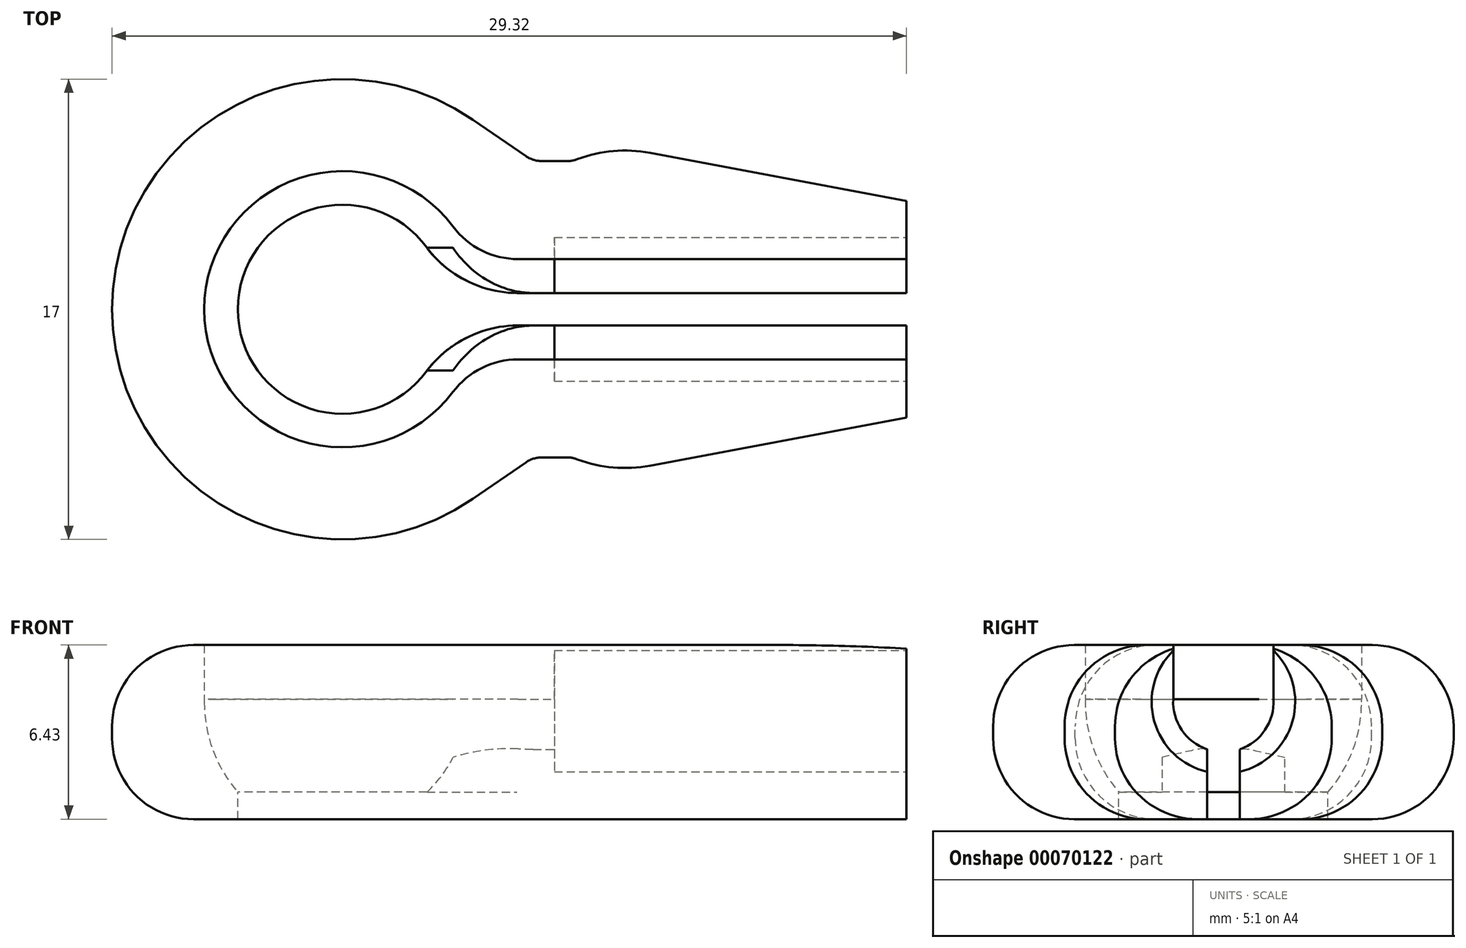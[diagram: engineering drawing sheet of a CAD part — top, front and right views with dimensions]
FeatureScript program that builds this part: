
annotation { "Feature Type Name" : "Feature", "Feature Type Description" : "" }
export const myFeature = defineFeature(function(context is Context, id is Id, definition is map)
    precondition{}
    {
        {
            assignVariable(context, id + "F0", {"name" : "ball", "anyValue" : 10});
        }
        {
            var Q0;
            Q0=qCreatedBy(makeId("Top.planeOp"),FACE);
            var sketch = newSketch(context, id + "F1", { "sketchPlane" : qUnion([Q0])});
            skCircle(sketch, "E0", {"center": v(0, 0) * mm, "radius": 5.1 * mm});
            skLineSegment(sketch, "E1", {"start": v(-13.72, 0) * mm, "end": v(11.71, 0) * mm});
            skCircle(sketch, "E2.0", {"center": v(0, 0) * mm, "radius": 8.5 * mm});
            skCircle(sketch, "E3", {"center": v(-8, 0) * mm, "radius": 2.9 * mm, "construction": true});
            skCircle(sketch, "E4", {"center": v(-8, 0) * mm, "radius": 1.4 * mm, "construction": true});
            skLineSegment(sketch, "E5.rect.bottom", {"start": v(4.82, 7) * mm, "end": v(20.82, 7) * mm});
            skLineSegment(sketch, "E5.rect.top", {"start": v(4.82, -7) * mm, "end": v(20.82, -7) * mm});
            skLineSegment(sketch, "E5.rect.left", {"start": v(4.82, 7) * mm, "end": v(4.82, -7) * mm, "construction": true});
            skLineSegment(sketch, "E5.rect.right", {"start": v(20.82, 7) * mm, "end": v(20.82, -7) * mm});
            skPoint(sketch, "E5.rect.middle", {"position": v(12.82, 0) * mm});
            skLineSegment(sketch, "E6", {"start": v(4.82, -7) * mm, "end": v(20.82, -4) * mm});
            skLineSegment(sketch, "E7.MirrorCS", {"start": v(4.82, 7) * mm, "end": v(20.82, 4) * mm});
            skSolve(sketch);
        }
        {
            var Q0;
            {var subQ0=sQuery(id+"F1.wireOp",EDGE,"E1");var subQ1=sQuery(id+"F1.wireOp",EDGE,"E0");var subQ2=makeQuery(id+"F1.imprint","INTERSECT",VERTEX,{"disambiguationData":[OD(0.0)],"derivedFrom":[subQ1,subQ0]});Q0=makeQuery(id+"F1.imprint","IMPRINT",FACE,{"disambiguationData":[TD([[makeQuery(id+"F1.imprint","IMPRINT",EDGE,{"disambiguationData":[TD([[subQ2,-1.0]])],"derivedFrom":subQ1}),-1.0]])]});}
            var Q1;
            {var subQ0=sQuery(id+"F1.wireOp",EDGE,"E1");var subQ1=sQuery(id+"F1.wireOp",EDGE,"E0");var subQ2=makeQuery(id+"F1.imprint","INTERSECT",VERTEX,{"disambiguationData":[OD(0.0)],"derivedFrom":[subQ1,subQ0]});Q1=makeQuery(id+"F1.imprint","IMPRINT",FACE,{"disambiguationData":[TD([[makeQuery(id+"F1.imprint","IMPRINT",EDGE,{"disambiguationData":[TD([[subQ2,1.0]])],"derivedFrom":subQ1}),-1.0]])]});}
            var Q2;
            {var subQ0=sQuery(id+"F1.wireOp",EDGE,"E2.0");var subQ1=sQuery(id+"F1.wireOp",EDGE,"E1");var subQ2=makeQuery(id+"F1.imprint","INTERSECT",VERTEX,{"disambiguationData":[OD(0.0)],"derivedFrom":[subQ1,subQ0]});Q2=makeQuery(id+"F1.imprint","IMPRINT",FACE,{"disambiguationData":[TD([[makeQuery(id+"F1.imprint","IMPRINT",EDGE,{"disambiguationData":[TD([[subQ2,1.0]])],"derivedFrom":subQ1}),1.0]])]});}
            var Q3;
            {var subQ0=sQuery(id+"F1.wireOp",EDGE,"E2.0");var subQ1=sQuery(id+"F1.wireOp",EDGE,"E1");var subQ2=makeQuery(id+"F1.imprint","INTERSECT",VERTEX,{"disambiguationData":[OD(0.0)],"derivedFrom":[subQ1,subQ0]});Q3=makeQuery(id+"F1.imprint","IMPRINT",FACE,{"disambiguationData":[TD([[makeQuery(id+"F1.imprint","IMPRINT",EDGE,{"disambiguationData":[TD([[subQ2,1.0]])],"derivedFrom":subQ1}),-1.0]])]});}
            var Q4;
            {var subQ0=sQuery(id+"F1.wireOp",EDGE,"E4");var subQ1=sQuery(id+"F1.wireOp",EDGE,"E1");var subQ2=makeQuery(id+"F1.imprint","INTERSECT",VERTEX,{"disambiguationData":[OD(1.0)],"derivedFrom":[subQ1,subQ0]});Q4=makeQuery(id+"F1.imprint","IMPRINT",FACE,{"disambiguationData":[TD([[makeQuery(id+"F1.imprint","IMPRINT",EDGE,{"disambiguationData":[TD([[subQ2,-1.0]])],"derivedFrom":subQ1}),1.0]])]});}
            var Q5;
            {var subQ0=sQuery(id+"F1.wireOp",EDGE,"E4");var subQ1=sQuery(id+"F1.wireOp",EDGE,"E1");var subQ2=makeQuery(id+"F1.imprint","INTERSECT",VERTEX,{"disambiguationData":[OD(1.0)],"derivedFrom":[subQ1,subQ0]});Q5=makeQuery(id+"F1.imprint","IMPRINT",FACE,{"disambiguationData":[TD([[makeQuery(id+"F1.imprint","IMPRINT",EDGE,{"disambiguationData":[TD([[subQ2,-1.0]])],"derivedFrom":subQ1}),-1.0]])]});}
            var Q6;
            {var subQ0=sQuery(id+"F1.wireOp",EDGE,"E1");var subQ1=sQuery(id+"F1.wireOp",EDGE,"E0");var subQ2=makeQuery(id+"F1.imprint","INTERSECT",VERTEX,{"disambiguationData":[OD(0.0)],"derivedFrom":[subQ1,subQ0]});Q6=makeQuery(id+"F1.imprint","IMPRINT",FACE,{"disambiguationData":[TD([[makeQuery(id+"F1.imprint","IMPRINT",EDGE,{"disambiguationData":[TD([[subQ2,1.0]])],"derivedFrom":subQ1}),1.0]])]});}
            var Q7;
            {var subQ0=sQuery(id+"F1.wireOp",EDGE,"E1");var subQ1=sQuery(id+"F1.wireOp",EDGE,"E0");var subQ2=makeQuery(id+"F1.imprint","INTERSECT",VERTEX,{"disambiguationData":[OD(0.0)],"derivedFrom":[subQ1,subQ0]});Q7=makeQuery(id+"F1.imprint","IMPRINT",FACE,{"disambiguationData":[TD([[makeQuery(id+"F1.imprint","IMPRINT",EDGE,{"disambiguationData":[TD([[subQ2,-1.0]])],"derivedFrom":subQ1}),1.0]])]});}
            var Q8;
            {var subQ0=sQuery(id+"F1.wireOp",EDGE,"E6");Q8=makeQuery(id+"F1.imprint","IMPRINT",FACE,{"disambiguationData":[TD([[makeQuery(id+"F1.imprint","IMPRINT",EDGE,{"derivedFrom":subQ0}),1.0]])]});}
            extrude(context, id + "F2", {"entities" : qUnion([Q0, Q1, Q2, Q3, Q4, Q5, Q6, Q7, Q8]), "depth" : 0.1 * mm, "hasSecondDirection" : true, "secondDirectionOppositeDirection" : true, "secondDirectionDepth" : (getVariable(context, 'ball') / 3) * mm});
        }
        {
            var Q0;
            {var subQ0=sQuery(id+"F1.wireOp",EDGE,"E1");var subQ1=sQuery(id+"F1.wireOp",EDGE,"E0");var subQ2=makeQuery(id+"F1.imprint","INTERSECT",VERTEX,{"disambiguationData":[OD(0.0)],"derivedFrom":[subQ1,subQ0]});Q0=makeQuery(id+"F1.imprint","IMPRINT",FACE,{"disambiguationData":[TD([[makeQuery(id+"F1.imprint","IMPRINT",EDGE,{"disambiguationData":[TD([[subQ2,-1.0]])],"derivedFrom":subQ1}),1.0]])]});}
            var Q1;
            Q1=sQuery(id+"F1.wireOp",EDGE,"E1");
            revolve(context, id + "F3", {"operationType" : NewBodyOperationType.REMOVE, "entities" : qUnion([Q0]), "axis" : qUnion([Q1]), "revolveType" : RevolveType.FULL, "oppositeDirection" : true});
        }
        {
            var Q0;
            Q0=makeQuery(id+"F2.opExtrude","SWEPT_FACE",FACE,{"disambiguationData":[OSD([sQuery(id+"F1.wireOp",EDGE,"E5.rect.right")])]});
            var sketch = newSketch(context, id + "F4", { "sketchPlane" : qUnion([Q0])});
            skArc(sketch, "E8", {"start": v(-1.85, 1.9) * mm, "mid": v(0, -2.65) * mm, "end": v(1.85, 1.9) * mm});
            skArc(sketch, "E9", {"start": v(-1.85, 0.1) * mm, "mid": v(0, -1.85) * mm, "end": v(1.85, 0.1) * mm});
            skLineSegment(sketch, "E10.bottom", {"start": v(1.85, 0.1) * mm, "end": v(-1.85, 0.1) * mm});
            skLineSegment(sketch, "E10.top", {"start": v(1.85, 5.18) * mm, "end": v(-1.85, 5.18) * mm});
            skLineSegment(sketch, "E10.left", {"start": v(1.85, 0.1) * mm, "end": v(1.85, 5.18) * mm});
            skLineSegment(sketch, "E10.right", {"start": v(-1.85, 0.1) * mm, "end": v(-1.85, 5.18) * mm});
            skPoint(sketch, "E10.middle", {"position": v(0, 2.64) * mm});
            skSolve(sketch);
        }
        {
            var Q0;
            Q0=makeQuery(id+"F2.opExtrude","CAP_FACE",FACE,{"disambiguationData":[OSD([sQuery(id+"F1.wireOp",EDGE,"E2.0"),sQuery(id+"F1.wireOp",EDGE,"E5.rect.right"),sQuery(id+"F1.wireOp",EDGE,"E6"),sQuery(id+"F1.wireOp",EDGE,"E7.MirrorCS")])],"isStart":false});
            var sketch = newSketch(context, id + "F5", { "sketchPlane" : qUnion([Q0])});
            skLineSegment(sketch, "E11", {"start": v(20.82, 0) * mm, "end": v(5.1, 0) * mm});
            skLineSegment(sketch, "E12", {"start": v(4.82, 7) * mm, "end": v(6.78, 5.65) * mm});
            skLineSegment(sketch, "E13", {"start": v(7.35, 5.47) * mm, "end": v(8.3, 5.47) * mm});
            skLineSegment(sketch, "E14", {"start": v(8.65, 5.54) * mm, "end": v(8.68, 5.55) * mm});
            skLineSegment(sketch, "E15.0", {"start": v(11.35, 5.78) * mm, "end": v(20.82, 4) * mm});
            skPoint(sketch, "E16.newPointA", {"position": v(4.82, 7) * mm});
            skPoint(sketch, "E16.newPointB", {"position": v(9.9, 6) * mm});
            skArc(sketch, "E16.filletArc", {"start": v(11.35, 5.78) * mm, "mid": v(10, 5.84) * mm, "end": v(8.68, 5.55) * mm});
            skPoint(sketch, "E17.visualSharp", {"position": v(8.49, 5.47) * mm});
            skArc(sketch, "E17.filletArc", {"start": v(8.3, 5.47) * mm, "mid": v(8.48, 5.49) * mm, "end": v(8.65, 5.54) * mm});
            skPoint(sketch, "E18.visualSharp", {"position": v(7.04, 5.47) * mm});
            skArc(sketch, "E18.filletArc", {"start": v(6.78, 5.65) * mm, "mid": v(7.05, 5.52) * mm, "end": v(7.35, 5.47) * mm});
            skLineSegment(sketch, "E19.MirrorCS", {"start": v(8.65, -5.54) * mm, "end": v(8.68, -5.55) * mm});
            skArc(sketch, "E20.MirrorCS", {"start": v(8.3, -5.47) * mm, "mid": v(8.48, -5.49) * mm, "end": v(8.65, -5.54) * mm});
            skArc(sketch, "E21.MirrorCS", {"start": v(6.78, -5.65) * mm, "mid": v(7.05, -5.52) * mm, "end": v(7.35, -5.47) * mm});
            skLineSegment(sketch, "E22.MirrorCS", {"start": v(7.35, -5.47) * mm, "end": v(8.3, -5.47) * mm});
            skLineSegment(sketch, "E23.MirrorCS", {"start": v(4.82, -7) * mm, "end": v(6.78, -5.65) * mm});
            skPoint(sketch, "E24.MirrorP", {"position": v(9.9, -6) * mm});
            skPoint(sketch, "E25.MirrorP", {"position": v(8.49, -5.47) * mm});
            skArc(sketch, "E26.MirrorCS", {"start": v(11.35, -5.78) * mm, "mid": v(10, -5.84) * mm, "end": v(8.68, -5.55) * mm});
            skPoint(sketch, "E27.MirrorP", {"position": v(7.04, -5.47) * mm});
            skPoint(sketch, "E28.MirrorP", {"position": v(4.82, -7) * mm});
            skSolve(sketch);
        }
        {
            var Q0;
            {var subQ1=sQuery(id+"F5.wireOp",EDGE,"E12");Q0=makeQuery(id+"F5.imprint","IMPRINT",FACE,{"disambiguationData":[TD([[makeQuery(id+"F5.imprint","IMPRINT",EDGE,{"derivedFrom":subQ1}),1.0]])]});}
            var Q1;
            Q1=makeQuery(id+"F5.imprint","IMPRINT",FACE,{"disambiguationData":[TD([[makeQuery(id+"F5.imprint","IMPRINT",EDGE,{"derivedFrom":sQuery(id+"F5.wireOp",EDGE,"E19.MirrorCS")}),-1.0]])]});
            extrude(context, id + "F6", {"entities" : qUnion([Q0, Q1]), "operationType" : NewBodyOperationType.REMOVE, "oppositeDirection" : true, "depth" : 25 * mm});
        }
        {
            var Q0;
            Q0=makeQuery(id+"F2.opExtrude","CAP_FACE",FACE,{"disambiguationData":[OSD([sQuery(id+"F1.wireOp",EDGE,"E2.0"),sQuery(id+"F1.wireOp",EDGE,"E4"),sQuery(id+"F1.wireOp",EDGE,"E5.rect.bottom"),sQuery(id+"F1.wireOp",EDGE,"E5.rect.top"),sQuery(id+"F1.wireOp",EDGE,"E5.rect.right")])],"isStart":false});
            var sketch = newSketch(context, id + "F7", { "sketchPlane" : qUnion([Q0])});
            skPoint(sketch, "E29.0", {"position": v(0, 0) * mm});
            skCircle(sketch, "E30", {"center": v(0, 0) * mm, "radius": 5.8 * mm, "construction": true});
            skCircle(sketch, "E31.0", {"center": v(0, 0) * mm, "radius": 6 * mm, "construction": true});
            skLineSegment(sketch, "E32.rect.bottom", {"start": v(-5.78, 0.5) * mm, "end": v(0.17, 0.5) * mm, "construction": true});
            skLineSegment(sketch, "E32.rect.top", {"start": v(-5.78, -0.5) * mm, "end": v(0.17, -0.5) * mm, "construction": true});
            skLineSegment(sketch, "E32.rect.left", {"start": v(-5.78, 0.5) * mm, "end": v(-5.78, -0.5) * mm, "construction": true});
            skLineSegment(sketch, "E32.rect.right", {"start": v(0.17, 0.5) * mm, "end": v(0.17, -0.5) * mm, "construction": true});
            skPoint(sketch, "E32.rect.middle", {"position": v(-2.8, 0) * mm});
            skLineSegment(sketch, "E33.bottom", {"start": v(20.82, 0.6) * mm, "end": v(-3.8, 0.6) * mm});
            skLineSegment(sketch, "E33.top", {"start": v(20.82, -0.6) * mm, "end": v(-3.8, -0.6) * mm});
            skLineSegment(sketch, "E33.left", {"start": v(20.82, 0.6) * mm, "end": v(20.82, -0.6) * mm});
            skLineSegment(sketch, "E33.right", {"start": v(-3.8, 0.6) * mm, "end": v(-3.8, -0.6) * mm});
            skPoint(sketch, "E33.middle", {"position": v(8.51, 0) * mm});
            skSolve(sketch);
        }
        {
            var Q0;
            Q0=makeQuery(id+"F2.opExtrude","CAP_FACE",FACE,{"disambiguationData":[OSD([sQuery(id+"F1.wireOp",EDGE,"E2.0"),sQuery(id+"F1.wireOp",EDGE,"E5.rect.bottom"),sQuery(id+"F1.wireOp",EDGE,"E5.rect.top"),sQuery(id+"F1.wireOp",EDGE,"E5.rect.right")])],"isStart":false});
            extrude(context, id + "F8", {"entities" : qUnion([Q0]), "operationType" : NewBodyOperationType.ADD, "depth" : 2 * mm});
        }
        {
            var Q0;
            {var subQ0=sQuery(id+"F7.wireOp",EDGE,"E33.left");Q0=makeQuery(id+"F7.imprint","IMPRINT",FACE,{"disambiguationData":[TD([[makeQuery(id+"F7.imprint","IMPRINT",EDGE,{"derivedFrom":subQ0}),-1.0]])]});}
            var Q1;
            {var subQ0=sQuery(id+"F7.wireOp",EDGE,"E33.right");Q1=makeQuery(id+"F7.imprint","IMPRINT",FACE,{"disambiguationData":[TD([[makeQuery(id+"F7.imprint","IMPRINT",EDGE,{"derivedFrom":subQ0}),1.0]])]});}
            extrude(context, id + "F9", {"entities" : qUnion([Q0, Q1]), "operationType" : NewBodyOperationType.REMOVE, "endBound" : BoundingType.SYMMETRIC, "oppositeDirection" : true, "depth" : 25 * mm});
        }
        {
            var Q0;
            Q0=makeQuery(id+"F4.imprint","IMPRINT",FACE,{"disambiguationData":[TD([[makeQuery(id+"F4.imprint","IMPRINT",EDGE,{"derivedFrom":sQuery(id+"F4.wireOp",EDGE,"E8")}),1.0]])]});
            var Q1;
            {var subQ0=sQuery(id+"F4.wireOp",EDGE,"E8");var subQ1=makeQuery(id+"F2.opExtrude","CAP_EDGE",EDGE,{"disambiguationData":[OSD([sQuery(id+"F1.wireOp",EDGE,"E5.rect.right")])],"isStart":false});var subQ2=makeQuery(id+"F4.imprint","INTERSECT",VERTEX,{"disambiguationData":[OD(0.0)],"derivedFrom":[subQ1,subQ0]});Q1=makeQuery(id+"F4.imprint","IMPRINT",FACE,{"disambiguationData":[TD([[makeQuery(id+"F4.imprint","IMPRINT",EDGE,{"disambiguationData":[TD([[subQ2,1.0]])],"derivedFrom":subQ0}),1.0]])]});}
            var Q2;
            {var subQ0=sQuery(id+"F4.wireOp",EDGE,"E10.left");var subQ1=sQuery(id+"F4.wireOp",EDGE,"E8");var subQ2=makeQuery(id+"F4.imprint","INTERSECT",VERTEX,{"derivedFrom":[subQ1,subQ0]});Q2=makeQuery(id+"F4.imprint","IMPRINT",FACE,{"disambiguationData":[TD([[makeQuery(id+"F4.imprint","IMPRINT",EDGE,{"disambiguationData":[TD([[subQ2,1.0]])],"derivedFrom":subQ1}),1.0]])]});}
            var Q3;
            {var subQ5=sQuery(id+"F4.wireOp",EDGE,"E9");Q3=makeQuery(id+"F4.imprint","IMPRINT",FACE,{"disambiguationData":[TD([[makeQuery(id+"F4.imprint","IMPRINT",EDGE,{"derivedFrom":subQ5}),-1.0]])]});}
            var Q4;
            {var subQ4=sQuery(id+"F4.wireOp",EDGE,"E10.bottom");Q4=makeQuery(id+"F4.imprint","IMPRINT",FACE,{"disambiguationData":[TD([[makeQuery(id+"F4.imprint","IMPRINT",EDGE,{"derivedFrom":subQ4}),-1.0]])]});}
            extrude(context, id + "F10", {"entities" : qUnion([Q0, Q1, Q2, Q3, Q4]), "operationType" : NewBodyOperationType.REMOVE, "oppositeDirection" : true, "depth" : 13 * mm});
        }
        {
            var Q0;
            {var subQ0=sQuery(id+"F1.wireOp",EDGE,"E5.rect.right");Q0=makeQuery(id+"F10.boolean.opBoolean","SPLIT",FACE,{"disambiguationData":[TD([makeQuery(id+"F10.opExtrude","SWEPT_FACE",FACE,{"disambiguationData":[OSD([sQuery(id+"F4.wireOp",EDGE,"E9")])]})])],"derivedFrom":makeQuery(id+"F2.opExtrude","SWEPT_FACE",FACE,{"disambiguationData":[OSD([subQ0])]})});}
            var Q1;
            {var subQ4=sQuery(id+"F4.wireOp",EDGE,"E10.bottom");Q1=makeQuery(id+"F4.imprint","IMPRINT",FACE,{"disambiguationData":[TD([[makeQuery(id+"F4.imprint","IMPRINT",EDGE,{"derivedFrom":subQ4}),-1.0]])]});}
            extrude(context, id + "F11", {"entities" : qUnion([Q0, Q1]), "operationType" : NewBodyOperationType.REMOVE, "oppositeDirection" : true, "depth" : 19.37 * mm});
        }
        {
            var Q0;
            Q0=makeQuery(id+"F11.boolean.opBoolean","INTERSECT",EDGE,{"derivedFrom":[makeQuery(id+"F3.boolean.opBoolean","COPY",FACE,{"derivedFrom":makeQuery(id+"F3.opRevolve","SWEPT_FACE",FACE,{"disambiguationData":[OSD([sQuery(id+"F1.wireOp",EDGE,"E0")])]})}),makeQuery(id+"F11.opExtrude","SWEPT_FACE",FACE,{"disambiguationData":[OSD([sQuery(id+"F4.wireOp",EDGE,"E9")])]})]});
            var Q1;
            Q1=makeQuery(id+"F11.boolean.opBoolean","INTERSECT",EDGE,{"derivedFrom":[makeQuery(id+"F8.opExtrude","SWEPT_FACE",FACE,{"disambiguationData":[OSD([sQuery(id+"F1.wireOp",EDGE,"E0"),sQuery(id+"F1.wireOp",EDGE,"E2.0"),sQuery(id+"F1.wireOp",EDGE,"E5.rect.bottom"),sQuery(id+"F1.wireOp",EDGE,"E5.rect.top"),sQuery(id+"F1.wireOp",EDGE,"E5.rect.right")])]}),makeQuery(id+"F11.opExtrude","SWEPT_FACE",FACE,{"disambiguationData":[OSD([sQuery(id+"F4.wireOp",EDGE,"E10.right")])]})]});
            var Q2;
            Q2=makeQuery(id+"F11.boolean.opBoolean","INTERSECT",EDGE,{"derivedFrom":[makeQuery(id+"F8.opExtrude","SWEPT_FACE",FACE,{"disambiguationData":[OSD([sQuery(id+"F1.wireOp",EDGE,"E0"),sQuery(id+"F1.wireOp",EDGE,"E2.0"),sQuery(id+"F1.wireOp",EDGE,"E5.rect.bottom"),sQuery(id+"F1.wireOp",EDGE,"E5.rect.top"),sQuery(id+"F1.wireOp",EDGE,"E5.rect.right")])]}),makeQuery(id+"F11.opExtrude","SWEPT_FACE",FACE,{"disambiguationData":[OSD([sQuery(id+"F4.wireOp",EDGE,"E10.left")])]})]});
            var Q3;
            Q3=makeQuery(id+"F9.boolean.opBoolean","INTERSECT",EDGE,{"derivedFrom":[makeQuery(id+"F3.boolean.opBoolean","COPY",FACE,{"derivedFrom":makeQuery(id+"F3.opRevolve","SWEPT_FACE",FACE,{"disambiguationData":[OSD([sQuery(id+"F1.wireOp",EDGE,"E0")])]})}),makeQuery(id+"F9.opExtrude","SWEPT_FACE",FACE,{"disambiguationData":[OSD([sQuery(id+"F7.wireOp",EDGE,"E33.top")])]})]});
            var Q4;
            Q4=makeQuery(id+"F9.boolean.opBoolean","INTERSECT",EDGE,{"derivedFrom":[makeQuery(id+"F3.boolean.opBoolean","COPY",FACE,{"derivedFrom":makeQuery(id+"F3.opRevolve","SWEPT_FACE",FACE,{"disambiguationData":[OSD([sQuery(id+"F1.wireOp",EDGE,"E0")])]})}),makeQuery(id+"F9.opExtrude","SWEPT_FACE",FACE,{"disambiguationData":[OSD([sQuery(id+"F7.wireOp",EDGE,"E33.bottom")])]})]});
            fillet(context, id + "F12", {"entities" : qUnion([Q0, Q1, Q2, Q3, Q4]), "radius" : 3 * mm, "tangentPropagation" : true, "allowEdgeOverflow" : false});
        }
        {
            var Q0;
            Q0=makeQuery(id+"F3.boolean.opBoolean","INTERSECT",EDGE,{"derivedFrom":[makeQuery(id+"F2.opExtrude","CAP_FACE",FACE,{"disambiguationData":[OSD([sQuery(id+"F1.wireOp",EDGE,"E2.0"),sQuery(id+"F1.wireOp",EDGE,"E5.rect.bottom"),sQuery(id+"F1.wireOp",EDGE,"E5.rect.top"),sQuery(id+"F1.wireOp",EDGE,"E5.rect.right")])],"isStart":false}),makeQuery(id+"F3.opRevolve","SWEPT_FACE",FACE,{"disambiguationData":[OSD([sQuery(id+"F1.wireOp",EDGE,"E0")])]})]});
            var Q1;
            Q1=makeQuery(id+"F12.opFillet","BLEND_EDGE",EDGE,{"blendedFrom":[makeQuery(id+"F10.boolean.opBoolean","INTERSECT",EDGE,{"disambiguationData":[OD(1.0)],"derivedFrom":[makeQuery(id+"F3.boolean.opBoolean","COPY",FACE,{"derivedFrom":makeQuery(id+"F3.opRevolve","SWEPT_FACE",FACE,{"disambiguationData":[OSD([sQuery(id+"F1.wireOp",EDGE,"E0")])]})}),makeQuery(id+"F10.opExtrude","SWEPT_FACE",FACE,{"disambiguationData":[OSD([sQuery(id+"F4.wireOp",EDGE,"E8")])]})]}),makeQuery(id+"F2.opExtrude","CAP_FACE",FACE,{"disambiguationData":[OSD([sQuery(id+"F1.wireOp",EDGE,"E2.0"),sQuery(id+"F1.wireOp",EDGE,"E5.rect.bottom"),sQuery(id+"F1.wireOp",EDGE,"E5.rect.top"),sQuery(id+"F1.wireOp",EDGE,"E5.rect.right")])],"isStart":false})],"blendedInto":[makeQuery(id+"F2.opExtrude","CAP_FACE",FACE,{"disambiguationData":[OSD([sQuery(id+"F1.wireOp",EDGE,"E2.0"),sQuery(id+"F1.wireOp",EDGE,"E5.rect.bottom"),sQuery(id+"F1.wireOp",EDGE,"E5.rect.top"),sQuery(id+"F1.wireOp",EDGE,"E5.rect.right")])],"isStart":false})]});
            var Q2;
            Q2=makeQuery(id+"F12.opFillet","BLEND_EDGE",EDGE,{"blendedFrom":[makeQuery(id+"F10.boolean.opBoolean","INTERSECT",EDGE,{"disambiguationData":[OD(0.0)],"derivedFrom":[makeQuery(id+"F3.boolean.opBoolean","COPY",FACE,{"derivedFrom":makeQuery(id+"F3.opRevolve","SWEPT_FACE",FACE,{"disambiguationData":[OSD([sQuery(id+"F1.wireOp",EDGE,"E0")])]})}),makeQuery(id+"F10.opExtrude","SWEPT_FACE",FACE,{"disambiguationData":[OSD([sQuery(id+"F4.wireOp",EDGE,"E8")])]})]}),makeQuery(id+"F2.opExtrude","CAP_FACE",FACE,{"disambiguationData":[OSD([sQuery(id+"F1.wireOp",EDGE,"E2.0"),sQuery(id+"F1.wireOp",EDGE,"E5.rect.bottom"),sQuery(id+"F1.wireOp",EDGE,"E5.rect.top"),sQuery(id+"F1.wireOp",EDGE,"E5.rect.right")])],"isStart":false})],"blendedInto":[makeQuery(id+"F2.opExtrude","CAP_FACE",FACE,{"disambiguationData":[OSD([sQuery(id+"F1.wireOp",EDGE,"E2.0"),sQuery(id+"F1.wireOp",EDGE,"E5.rect.bottom"),sQuery(id+"F1.wireOp",EDGE,"E5.rect.top"),sQuery(id+"F1.wireOp",EDGE,"E5.rect.right")])],"isStart":false})]});
            var Q3;
            Q3=makeQuery(id+"F9.boolean.opBoolean","COPY",EDGE,{"derivedFrom":makeQuery(id+"F9.opExtrude","CAP_EDGE",EDGE,{"disambiguationData":[OSD([sQuery(id+"F7.wireOp",EDGE,"E33.bottom")])],"isStart":true})});
            var Q4;
            Q4=makeQuery(id+"F9.boolean.opBoolean","COPY",EDGE,{"derivedFrom":makeQuery(id+"F9.opExtrude","CAP_EDGE",EDGE,{"disambiguationData":[OSD([sQuery(id+"F7.wireOp",EDGE,"E33.top")])],"isStart":true})});
            fillet(context, id + "F13", {"entities" : qUnion([Q0, Q1, Q2, Q3, Q4]), "radius" : 0.4 * mm, "tangentPropagation" : true, "allowEdgeOverflow" : false});
        }
        {
            var Q0;
            Q0=makeQuery(id+"F2.opExtrude","CAP_FACE",FACE,{"disambiguationData":[OSD([sQuery(id+"F1.wireOp",EDGE,"E2.0"),sQuery(id+"F1.wireOp",EDGE,"E5.rect.right"),sQuery(id+"F1.wireOp",EDGE,"E6"),sQuery(id+"F1.wireOp",EDGE,"E7.MirrorCS")])],"isStart":true});
            extrude(context, id + "F14", {"entities" : qUnion([Q0]), "operationType" : NewBodyOperationType.ADD, "depth" : 1 * mm});
        }
        {
            var Q0;
            {var subQ0=sQuery(id+"F1.wireOp",EDGE,"E2.0");Q0=makeQuery(id+"FxmCNC86uWfBR2P_1.opChamfer","BLEND_EDGE",EDGE,{"blendedFrom":[makeQuery(id+"F8.opExtrude","CAP_EDGE",EDGE,{"disambiguationData":[OSD([subQ0])],"isStart":false}),makeQuery(id+"F8.boolean.opBoolean","MERGE",FACE,{"derivedFrom":[makeQuery(id+"F2.opExtrude","SWEPT_FACE",FACE,{"disambiguationData":[OSD([subQ0])]}),makeQuery(id+"F8.opExtrude","SWEPT_FACE",FACE,{"disambiguationData":[OSD([subQ0])]})]})],"blendedInto":[makeQuery(id+"F8.boolean.opBoolean","MERGE",FACE,{"derivedFrom":[makeQuery(id+"F2.opExtrude","SWEPT_FACE",FACE,{"disambiguationData":[OSD([subQ0])]}),makeQuery(id+"F8.opExtrude","SWEPT_FACE",FACE,{"disambiguationData":[OSD([subQ0])]})]})]});}
            var Q1;
            Q1=makeQuery(id+"F8.opExtrude","CAP_EDGE",EDGE,{"disambiguationData":[OSD([sQuery(id+"F1.wireOp",EDGE,"E7.MirrorCS")])],"isStart":false});
            var Q2;
            Q2=makeQuery(id+"F8.opExtrude","CAP_EDGE",EDGE,{"disambiguationData":[OSD([sQuery(id+"F1.wireOp",EDGE,"E6")])],"isStart":false});
            var Q3;
            Q3=makeQuery(id+"F14.opExtrude","CAP_EDGE",EDGE,{"disambiguationData":[OSD([sQuery(id+"F1.wireOp",EDGE,"E7.MirrorCS")])],"isStart":false});
            var Q4;
            Q4=makeQuery(id+"F14.opExtrude","CAP_EDGE",EDGE,{"disambiguationData":[OSD([sQuery(id+"F1.wireOp",EDGE,"E6")])],"isStart":false});
            fillet(context, id + "F15", {"entities" : qUnion([Q0, Q1, Q2, Q3, Q4]), "radius" : 3 * mm, "tangentPropagation" : true, "allowEdgeOverflow" : false});
        }
    });
